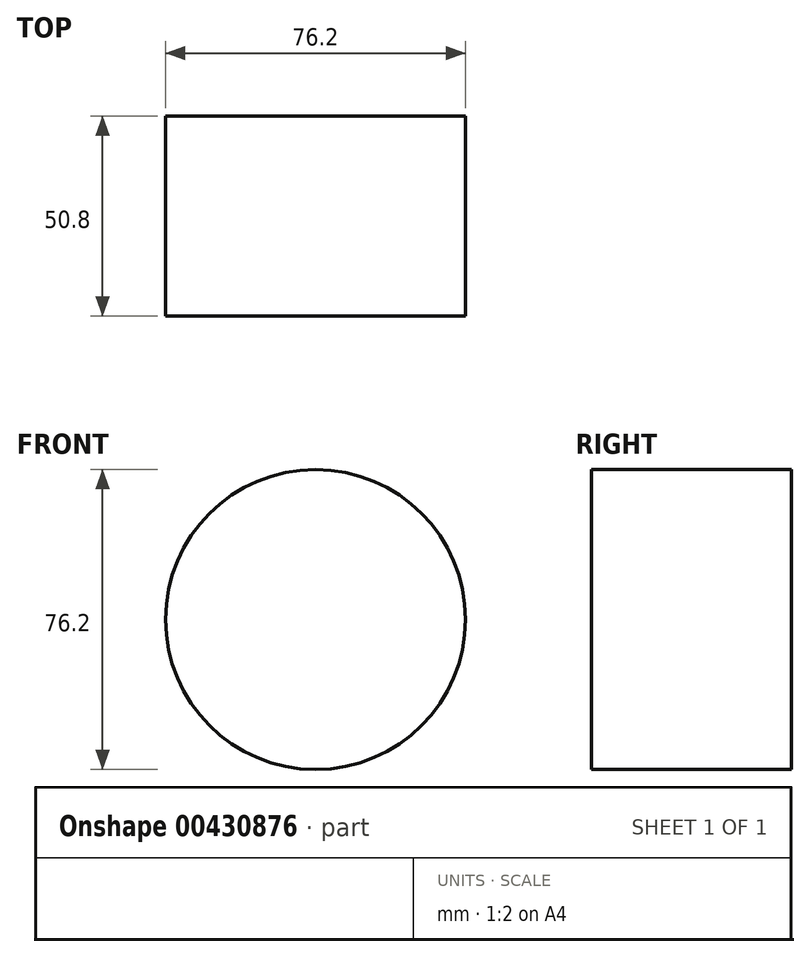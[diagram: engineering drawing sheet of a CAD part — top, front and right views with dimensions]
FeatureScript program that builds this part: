
annotation { "Feature Type Name" : "Feature", "Feature Type Description" : "" }
export const myFeature = defineFeature(function(context is Context, id is Id, definition is map)
    precondition{}
    {
        {
            var Q0;
            Q0=qCreatedBy(makeId("Front.planeOp"),FACE);
            var sketch = newSketch(context, id + "F0", { "sketchPlane" : qUnion([Q0])});
            skCircle(sketch, "E0", {"center": v(0, 0) * mm, "radius": 38.1 * mm});
            skSolve(sketch);
        }
        {
            var Q0;
            Q0=makeQuery(id+"F0.imprint","IMPRINT",FACE,{"disambiguationData":[TD([[makeQuery(id+"F0.imprint","IMPRINT",EDGE,{"derivedFrom":sQuery(id+"F0.wireOp",EDGE,"E0")}),1.0]])]});
            var Q1;
            Q1=sQuery(id+"F0.wireOp",EDGE,"E0");
            extrude(context, id + "F1", {"entities" : qUnion([Q0]), "surfaceEntities" : qUnion([Q1]), "endBound" : BoundingType.SYMMETRIC, "depth" : 50.8 * mm});
        }
    });
